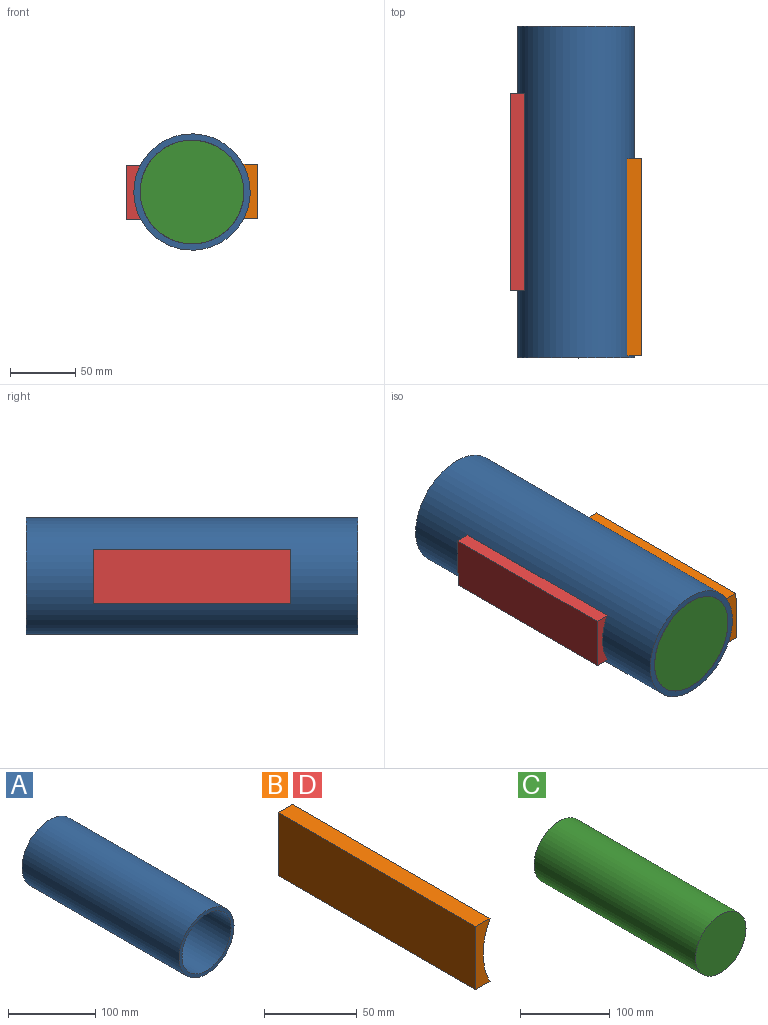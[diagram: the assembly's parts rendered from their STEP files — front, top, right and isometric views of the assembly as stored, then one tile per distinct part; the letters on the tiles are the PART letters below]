
ASSEMBLY  parts=4 mates=4
PART A: 4 faces, bbox 89x254x89 mm
  f0: cylinder r=39.7mm len=254mm, axis (0,1,0), area 63358.4mm2, adj f2,f3
  f1: cylinder r=44.5mm len=254mm, axis (0,1,0), area 71018.8mm2, adj f2,f3
  f2: plane 89x89mm, normal (0,-1,0), area 1269.7mm2, adj f0,f1
  f3: plane 89x89mm, normal (0,1,0), area 1269.7mm2, adj f0,f1
PART B: 6 faces, bbox 10.9x150.9x41.7 mm
  f0: plane 150.9x41.66mm, normal (-1,0,0), area 6286.5mm2, adj f1,f3,f4,f5
  f1: plane 150.9x10.92mm, normal (0,0,-1), area 1647.8mm2, adj f0,f2,f4,f5
  f2: cylinder r=44.45mm len=150.9mm, axis (0,1,0), area 6542.8mm2, adj f1,f3,f4,f5
  f3: plane 150.9x10.92mm, normal (0,0,1), area 1647.8mm2, adj f0,f2,f4,f5
  f4: plane 41.66x10.92mm, normal (0,-1,0), area 309.2mm2, adj f0,f1,f2,f3
  f5: plane 41.66x10.92mm, normal (0,1,0), area 309.2mm2, adj f0,f1,f2,f3
PART C: 3 faces, bbox 79.4x254x79.4 mm
  f0: cylinder r=39.7mm len=254mm, axis (0,-1,0), area 63360.7mm2, adj f1,f2
  f1: plane 79.4x79.4mm, normal (0,1,0), area 4951.8mm2, adj f0
  f2: plane 79.4x79.4mm, normal (0,-1,0), area 4951.8mm2, adj f0
PART D: same geometry as B
PLACE A rot(axis=(0,1,0),96.8deg) t=(-45.23,222.01,-94.44)mm fixed
PLACE B rot(axis=(0,1,0),179.3deg) t=(4.72,120.53,-73.03)mm
PLACE C rot(axis=(0,1,0),94.7deg) t=(-45.23,222.01,-94.44)mm
PLACE D rot(axis=(0,-1,0),0.6deg) t=(-95.18,170.52,-115.82)mm
MATE parallel D.f2 <-> B.f2  axis (0,1,0) through (-45.23,170.52,-94.44)mm
MATE revolute C.f0 <-> A.f1  axis (0,1,0) through (-45.23,222.01,-94.44)mm
MATE cylindrical D.f2 <-> A.f1  axis (0,1,0) through (-45.23,95.07,-94.44)mm
MATE cylindrical B.f2 <-> A.f1  axis (0,1,0) through (-45.23,45.08,-94.44)mm
